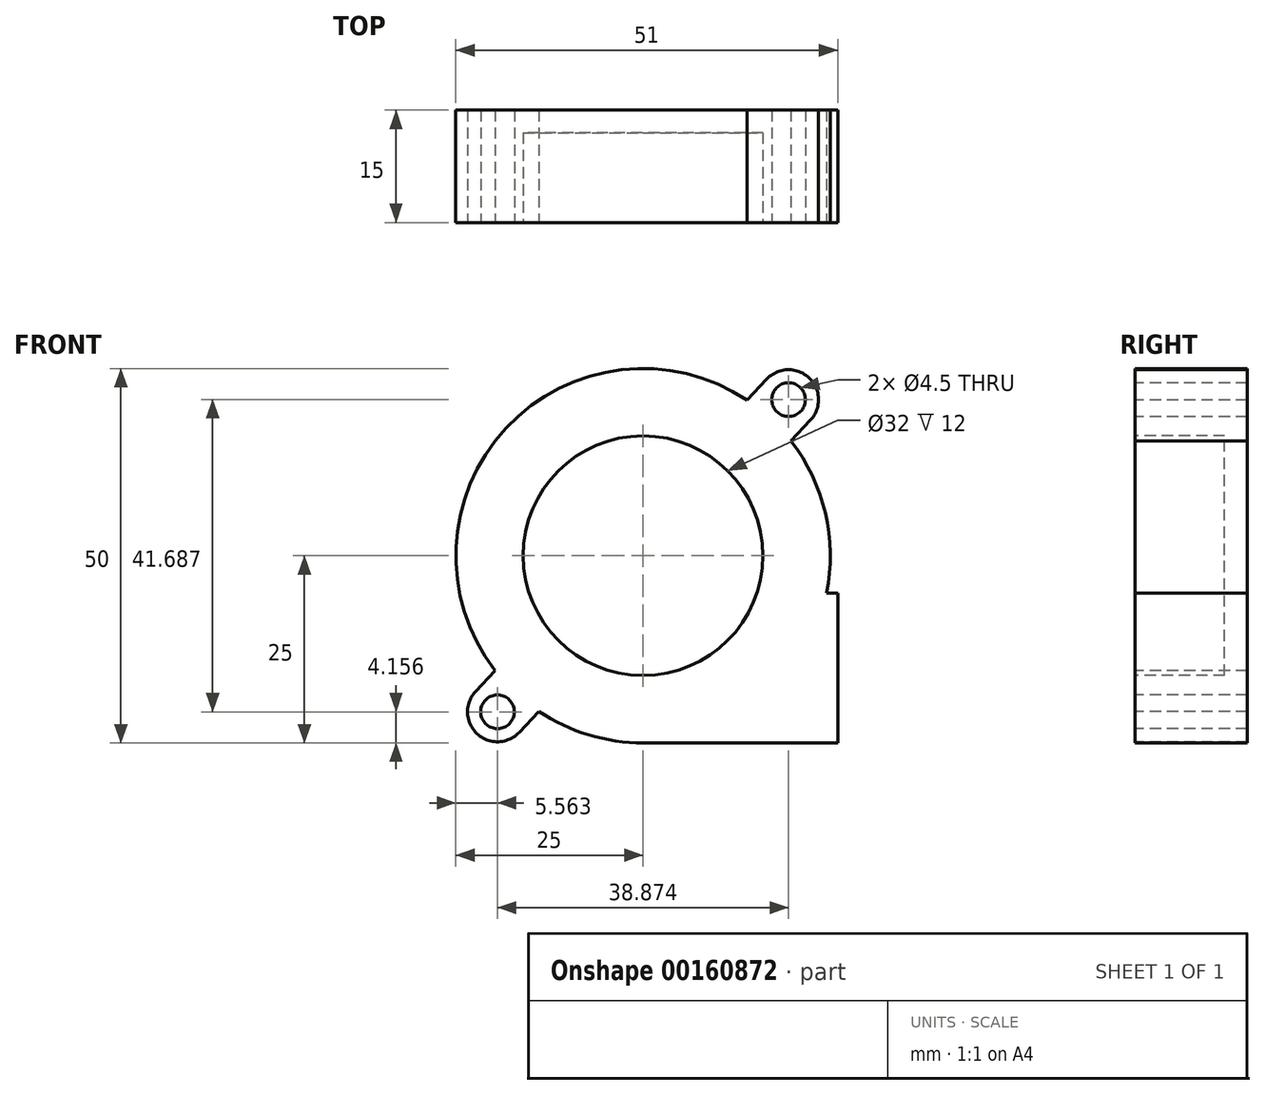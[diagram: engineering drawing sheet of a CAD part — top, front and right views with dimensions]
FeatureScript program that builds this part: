
annotation { "Feature Type Name" : "Feature", "Feature Type Description" : "" }
export const myFeature = defineFeature(function(context is Context, id is Id, definition is map)
    precondition{}
    {
        {
            var Q0;
            Q0=qCreatedBy(makeId("Front.planeOp"),FACE);
            var sketch = newSketch(context, id + "F0", { "sketchPlane" : qUnion([Q0])});
            skArc(sketch, "E0", {"start": v(24.5, -5) * mm, "mid": v(24.35, 5.68) * mm, "end": v(19.76, 15.32) * mm});
            skLineSegment(sketch, "E1", {"start": v(0, -25) * mm, "end": v(26, -25) * mm});
            skLineSegment(sketch, "E2", {"start": v(26, -25) * mm, "end": v(26, -5) * mm});
            skLineSegment(sketch, "E3", {"start": v(26, -5) * mm, "end": v(24.5, -5) * mm});
            skLineSegment(sketch, "E4", {"start": v(0, 0) * mm, "end": v(-19.44, -20.84) * mm, "construction": true});
            skCircle(sketch, "E5", {"center": v(-19.44, -20.84) * mm, "radius": 2.25 * mm});
            skArc(sketch, "E6", {"start": v(-22.36, -18.12) * mm, "mid": v(-22.16, -23.77) * mm, "end": v(-16.51, -23.57) * mm});
            skLineSegment(sketch, "E7", {"start": v(-19.44, -20.84) * mm, "end": v(-22.36, -18.12) * mm, "construction": true});
            skLineSegment(sketch, "E8", {"start": v(-22.36, -18.12) * mm, "end": v(-19.76, -15.32) * mm});
            skLineSegment(sketch, "E9.MirrorCS", {"start": v(-16.51, -23.57) * mm, "end": v(-13.9, -20.78) * mm});
            skLineSegment(sketch, "E10", {"start": v(0, 0) * mm, "end": v(3.82, -3.56) * mm, "construction": true});
            skLineSegment(sketch, "E11.MirrorCS", {"start": v(16.51, 23.57) * mm, "end": v(13.9, 20.78) * mm});
            skArc(sketch, "E12.MirrorCS", {"start": v(16.51, 23.57) * mm, "mid": v(22.16, 23.77) * mm, "end": v(22.36, 18.12) * mm});
            skLineSegment(sketch, "E13.MirrorCS", {"start": v(22.36, 18.12) * mm, "end": v(19.76, 15.32) * mm});
            skCircle(sketch, "E14.MirrorC", {"center": v(19.44, 20.84) * mm, "radius": 2.25 * mm});
            skArc(sketch, "E15.trimOffspring", {"start": v(-13.9, -20.78) * mm, "mid": v(-7.27, -23.92) * mm, "end": v(0, -25) * mm});
            skArc(sketch, "E16.trimOffspring", {"start": v(13.9, 20.78) * mm, "mid": v(-18.28, 17.05) * mm, "end": v(-19.76, -15.32) * mm});
            skSolve(sketch);
        }
        {
            var Q0;
            Q0 = qSketchRegion(id + "F0", true);
            extrude(context, id + "F1", {"entities" : qUnion([Q0]), "oppositeDirection" : true, "depth" : 15 * mm});
        }
        {
            var Q0;
            Q0=makeQuery(id+"F1.opExtrude","CAP_FACE",FACE,{"disambiguationData":[OSD([sQuery(id+"F0.wireOp",EDGE,"E0"),sQuery(id+"F0.wireOp",EDGE,"E1"),sQuery(id+"F0.wireOp",EDGE,"E2"),sQuery(id+"F0.wireOp",EDGE,"E3"),sQuery(id+"F0.wireOp",EDGE,"E5"),sQuery(id+"F0.wireOp",EDGE,"E6"),sQuery(id+"F0.wireOp",EDGE,"E8"),sQuery(id+"F0.wireOp",EDGE,"E9.MirrorCS"),sQuery(id+"F0.wireOp",EDGE,"E11.MirrorCS"),sQuery(id+"F0.wireOp",EDGE,"E12.MirrorCS"),sQuery(id+"F0.wireOp",EDGE,"E13.MirrorCS"),sQuery(id+"F0.wireOp",EDGE,"E14.MirrorC"),sQuery(id+"F0.wireOp",EDGE,"E15.trimOffspring"),sQuery(id+"F0.wireOp",EDGE,"E16.trimOffspring")])],"isStart":true});
            var sketch = newSketch(context, id + "F2", { "sketchPlane" : qUnion([Q0])});
            skCircle(sketch, "E17", {"center": v(0, 0) * mm, "radius": 16 * mm});
            skSolve(sketch);
        }
        {
            var Q0;
            Q0 = qSketchRegion(id + "F2", true);
            extrude(context, id + "F3", {"entities" : qUnion([Q0]), "operationType" : NewBodyOperationType.REMOVE, "oppositeDirection" : true, "depth" : 12 * mm});
        }
    });
